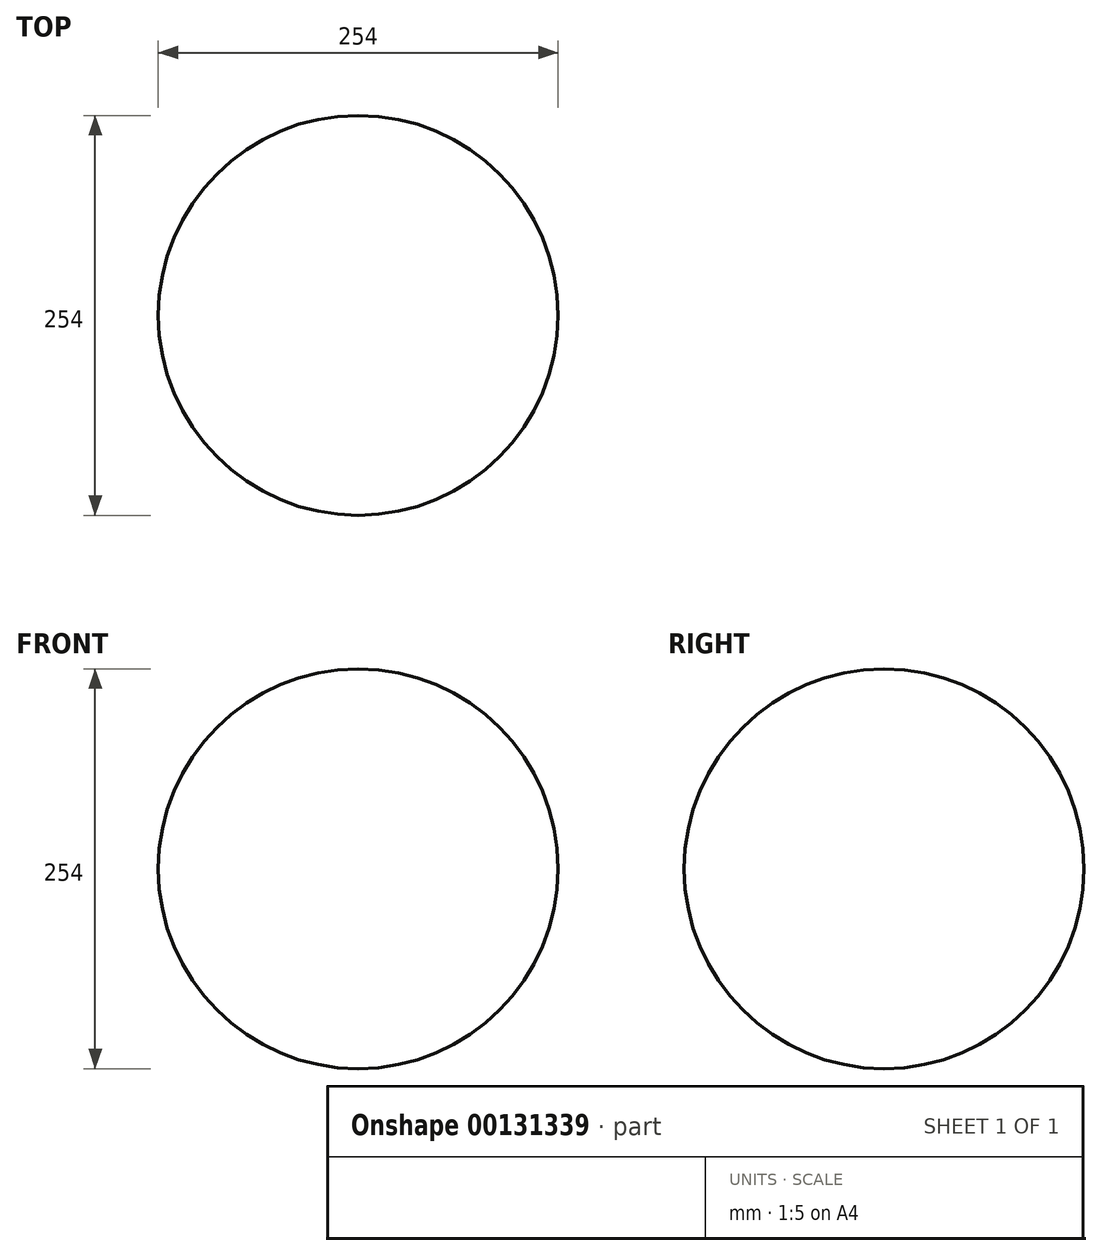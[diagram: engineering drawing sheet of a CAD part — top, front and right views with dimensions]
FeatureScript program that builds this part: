
annotation { "Feature Type Name" : "Feature", "Feature Type Description" : "" }
export const myFeature = defineFeature(function(context is Context, id is Id, definition is map)
    precondition{}
    {
        {
            var Q0;
            Q0=qCreatedBy(makeId("Front.planeOp"),FACE);
            var sketch = newSketch(context, id + "F0", { "sketchPlane" : qUnion([Q0])});
            skCircle(sketch, "E0", {"center": v(0, 0) * mm, "radius": 127 * mm});
            skLineSegment(sketch, "E1", {"start": v(-127, 0) * mm, "end": v(127, 0) * mm});
            skSolve(sketch);
        }
        {
            var Q0;
            {var subQ0=sQuery(id+"F0.wireOp",EDGE,"E1");Q0=makeQuery(id+"F0.imprint","IMPRINT",FACE,{"disambiguationData":[TD([[makeQuery(id+"F0.imprint","IMPRINT",EDGE,{"derivedFrom":subQ0}),-1.0]])]});}
            var Q1;
            Q1=sQuery(id+"F0.wireOp",EDGE,"E1");
            revolve(context, id + "F1", {"entities" : qUnion([Q0]), "axis" : qUnion([Q1]), "revolveType" : RevolveType.FULL});
        }
    });
